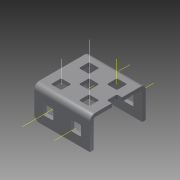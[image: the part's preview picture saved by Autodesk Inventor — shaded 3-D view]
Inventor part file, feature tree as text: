
AUTODESK INVENTOR PART (.ipt)
format: ipt  version: 2015 SP1 (Build 190203100, 203)  size: 1,904,128 bytes
history: native  units: in
note: dims shown in document units (in); Inventor stores cm internally (conversion verified against a paired STEP export)
features: other x16, pattern_linear x3, sheet_metal_op x1, extrude x1, imported_body x1, sketch x1
ambient origin geometry x8: Origin, YZ Plane, XZ Plane, XY Plane, X Axis, Y Axis, Z Axis, Center Point
bodies: Body1 (feature_tree)
feature tree (23):
  sheet_metal_op  "Fold1"
  other  "C-Channel"
  extrude  "length cut"  Depth=0.5in
  other  "top axis"
  other  "inner axis"
  other  "front axis"
  other  "back axis"
  pattern_linear  "top axes"  Spacing1=0.5in  [1 undecoded]
  pattern_linear  "inner axes"  Spacing1=0.5in  [1 undecoded]
  pattern_linear  "horiz axes"  Spacing1=-1.0in  [1 undecoded]
  other  "right plane"
  imported_body  "Base1"
  sketch  "Sketch1"  dims[d1=0.0in d4=0.5in d5=0.7874in d7=0.5in d10=0.5in d13=0.5in d14=-1.0in d15=0.0in d16=0.0in d17=0.0in d18=0.0in d19=0.0in]
  other  "Work Point1"
  other  "Work Point2"
  other  "Work Point3"
  other  "Work Point4"
  other  "Work Axis5"
  other  "Work Axis11"
  other  "Work Axis12"
  other  "Work Axis23"
  other  "Work Axis30"
  other  "left plane"
note: 3 required parameter values undecoded (feature->parameter linkage not recoverable at this tier; creation-order binding heuristic only, values carry confidence <= 0.55)
